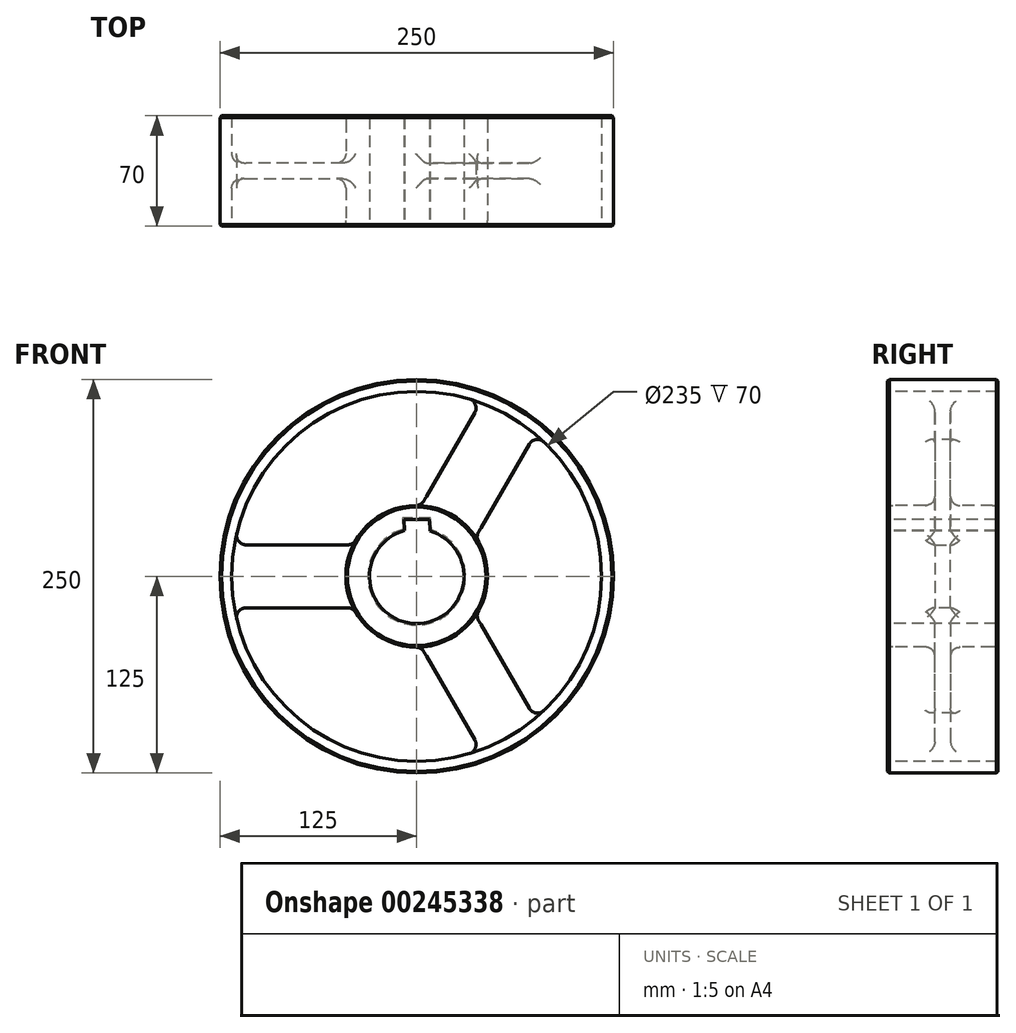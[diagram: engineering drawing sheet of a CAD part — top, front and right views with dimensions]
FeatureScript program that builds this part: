
annotation { "Feature Type Name" : "Feature", "Feature Type Description" : "" }
export const myFeature = defineFeature(function(context is Context, id is Id, definition is map)
    precondition{}
    {
        {
            var Q0;
            Q0=qCreatedBy(makeId("Front.planeOp"),FACE);
            var sketch = newSketch(context, id + "F0", { "sketchPlane" : qUnion([Q0])});
            skCircle(sketch, "E0", {"center": v(0, 0) * mm, "radius": 125 * mm});
            skSolve(sketch);
        }
        {
            var Q0;
            Q0 = qSketchRegion(id + "F0", true);
            extrude(context, id + "F1", {"entities" : qUnion([Q0]), "depth" : 70 * mm});
        }
        {
            var Q0;
            Q0=makeQuery(id+"F1.opExtrude","CAP_FACE",FACE,{"disambiguationData":[OSD([sQuery(id+"F0.wireOp",EDGE,"E0")])],"isStart":false});
            var sketch = newSketch(context, id + "F2", { "sketchPlane" : qUnion([Q0])});
            skCircle(sketch, "E1", {"center": v(0, 0) * mm, "radius": 117.5 * mm});
            skSolve(sketch);
        }
        {
            var Q0;
            Q0 = qSketchRegion(id + "F2", true);
            extrude(context, id + "F3", {"entities" : qUnion([Q0]), "operationType" : NewBodyOperationType.REMOVE, "oppositeDirection" : true, "depth" : 30 * mm});
        }
        {
            var Q0;
            Q0=makeQuery(id+"F1.opExtrude","CAP_FACE",FACE,{"disambiguationData":[OSD([sQuery(id+"F0.wireOp",EDGE,"E0")])],"isStart":true});
            var sketch = newSketch(context, id + "F4", { "sketchPlane" : qUnion([Q0])});
            skCircle(sketch, "E2", {"center": v(0, 0) * mm, "radius": 117.5 * mm});
            skSolve(sketch);
        }
        {
            var Q0;
            Q0 = qSketchRegion(id + "F4", true);
            extrude(context, id + "F5", {"entities" : qUnion([Q0]), "operationType" : NewBodyOperationType.REMOVE, "oppositeDirection" : true, "depth" : 30 * mm});
        }
        {
            var Q0;
            Q0=makeQuery(id+"F5.boolean.opBoolean","COPY",FACE,{"derivedFrom":makeQuery(id+"F5.opExtrude","CAP_FACE",FACE,{"disambiguationData":[OSD([sQuery(id+"F4.wireOp",EDGE,"E2")])],"isStart":false})});
            var sketch = newSketch(context, id + "F6", { "sketchPlane" : qUnion([Q0])});
            skCircle(sketch, "E3", {"center": v(0, 0) * mm, "radius": 45 * mm});
            skSolve(sketch);
        }
        {
            var Q0;
            Q0 = qSketchRegion(id + "F6", true);
            extrude(context, id + "F7", {"entities" : qUnion([Q0]), "operationType" : NewBodyOperationType.ADD, "depth" : 30 * mm});
        }
        {
            var Q0;
            Q0=makeQuery(id+"F3.boolean.opBoolean","COPY",FACE,{"derivedFrom":makeQuery(id+"F3.opExtrude","CAP_FACE",FACE,{"disambiguationData":[OSD([sQuery(id+"F2.wireOp",EDGE,"E1")])],"isStart":false})});
            var sketch = newSketch(context, id + "F8", { "sketchPlane" : qUnion([Q0])});
            skCircle(sketch, "E4", {"center": v(0, 0) * mm, "radius": 45 * mm});
            skSolve(sketch);
        }
        {
            var Q0;
            Q0 = qSketchRegion(id + "F8", true);
            extrude(context, id + "F9", {"entities" : qUnion([Q0]), "operationType" : NewBodyOperationType.ADD, "depth" : 30 * mm});
        }
        {
            var Q0;
            Q0=makeQuery(id+"F9.opExtrude","CAP_FACE",FACE,{"disambiguationData":[OSD([sQuery(id+"F8.wireOp",EDGE,"E4")])],"isStart":false});
            var sketch = newSketch(context, id + "F10", { "sketchPlane" : qUnion([Q0])});
            skArc(sketch, "E5", {"start": v(-7.63, 29.01) * mm, "mid": v(-0.39, -30) * mm, "end": v(8.38, 28.8) * mm});
            skLineSegment(sketch, "E6.bottom", {"start": v(-8, 36) * mm, "end": v(8, 36) * mm});
            skLineSegment(sketch, "E6.left", {"start": v(-8, 36) * mm, "end": v(-7.63, 29.01) * mm});
            skLineSegment(sketch, "E6.right", {"start": v(8, 36) * mm, "end": v(8.38, 28.8) * mm});
            skSolve(sketch);
        }
        {
            var Q0;
            Q0=makeQuery(id+"F10.imprint","IMPRINT",FACE,{"disambiguationData":[TD([[makeQuery(id+"F10.imprint","IMPRINT",EDGE,{"derivedFrom":sQuery(id+"F10.wireOp",EDGE,"E5")}),1.0]])]});
            extrude(context, id + "F11", {"entities" : qUnion([Q0]), "operationType" : NewBodyOperationType.REMOVE, "endBound" : BoundingType.THROUGH_ALL, "oppositeDirection" : true, "depth" : 25 * mm});
        }
        {
            var Q0;
            Q0=makeQuery(id+"F1.opExtrude","CAP_EDGE",EDGE,{"disambiguationData":[OSD([sQuery(id+"F0.wireOp",EDGE,"E0")])],"isStart":false});
            var Q1;
            Q1=makeQuery(id+"F3.boolean.opBoolean","COPY",EDGE,{"derivedFrom":makeQuery(id+"F3.opExtrude","CAP_EDGE",EDGE,{"disambiguationData":[OSD([sQuery(id+"F2.wireOp",EDGE,"E1")])],"isStart":true})});
            var Q2;
            Q2=makeQuery(id+"F9.opExtrude","CAP_EDGE",EDGE,{"disambiguationData":[OSD([sQuery(id+"F8.wireOp",EDGE,"E4")])],"isStart":false});
            var Q3;
            Q3=makeQuery(id+"F11.boolean.opBoolean","COPY",EDGE,{"derivedFrom":makeQuery(id+"F11.opExtrude","CAP_EDGE",EDGE,{"disambiguationData":[OSD([sQuery(id+"F10.wireOp",EDGE,"E5")])],"isStart":true})});
            var Q4;
            Q4=makeQuery(id+"F11.boolean.opBoolean","COPY",EDGE,{"derivedFrom":makeQuery(id+"F11.opExtrude","CAP_EDGE",EDGE,{"disambiguationData":[OSD([sQuery(id+"F10.wireOp",EDGE,"E6.left")])],"isStart":true})});
            var Q5;
            Q5=makeQuery(id+"F11.boolean.opBoolean","COPY",EDGE,{"derivedFrom":makeQuery(id+"F11.opExtrude","CAP_EDGE",EDGE,{"disambiguationData":[OSD([sQuery(id+"F10.wireOp",EDGE,"E6.bottom")])],"isStart":true})});
            var Q6;
            Q6=makeQuery(id+"F11.boolean.opBoolean","COPY",EDGE,{"derivedFrom":makeQuery(id+"F11.opExtrude","CAP_EDGE",EDGE,{"disambiguationData":[OSD([sQuery(id+"F10.wireOp",EDGE,"E6.right")])],"isStart":true})});
            var Q7;
            Q7=makeQuery(id+"F1.opExtrude","CAP_EDGE",EDGE,{"disambiguationData":[OSD([sQuery(id+"F0.wireOp",EDGE,"E0")])],"isStart":true});
            var Q8;
            Q8=makeQuery(id+"F5.boolean.opBoolean","COPY",EDGE,{"derivedFrom":makeQuery(id+"F5.opExtrude","CAP_EDGE",EDGE,{"disambiguationData":[OSD([sQuery(id+"F4.wireOp",EDGE,"E2")])],"isStart":true})});
            var Q9;
            Q9=makeQuery(id+"F7.opExtrude","CAP_EDGE",EDGE,{"disambiguationData":[OSD([sQuery(id+"F6.wireOp",EDGE,"E3")])],"isStart":false});
            var Q10;
            Q10=makeQuery(id+"F11.boolean.opBoolean","INTERSECT",EDGE,{"derivedFrom":[makeQuery(id+"F7.opExtrude","CAP_FACE",FACE,{"disambiguationData":[OSD([sQuery(id+"F6.wireOp",EDGE,"E3")])],"isStart":false}),makeQuery(id+"F11.opExtrude","SWEPT_FACE",FACE,{"disambiguationData":[OSD([sQuery(id+"F10.wireOp",EDGE,"E5")])]})]});
            var Q11;
            Q11=makeQuery(id+"F11.boolean.opBoolean","INTERSECT",EDGE,{"derivedFrom":[makeQuery(id+"F7.opExtrude","CAP_FACE",FACE,{"disambiguationData":[OSD([sQuery(id+"F6.wireOp",EDGE,"E3")])],"isStart":false}),makeQuery(id+"F11.opExtrude","SWEPT_FACE",FACE,{"disambiguationData":[OSD([sQuery(id+"F10.wireOp",EDGE,"E6.right")])]})]});
            var Q12;
            Q12=makeQuery(id+"F11.boolean.opBoolean","INTERSECT",EDGE,{"derivedFrom":[makeQuery(id+"F7.opExtrude","CAP_FACE",FACE,{"disambiguationData":[OSD([sQuery(id+"F6.wireOp",EDGE,"E3")])],"isStart":false}),makeQuery(id+"F11.opExtrude","SWEPT_FACE",FACE,{"disambiguationData":[OSD([sQuery(id+"F10.wireOp",EDGE,"E6.left")])]})]});
            var Q13;
            Q13=makeQuery(id+"F11.boolean.opBoolean","INTERSECT",EDGE,{"derivedFrom":[makeQuery(id+"F7.opExtrude","CAP_FACE",FACE,{"disambiguationData":[OSD([sQuery(id+"F6.wireOp",EDGE,"E3")])],"isStart":false}),makeQuery(id+"F11.opExtrude","SWEPT_FACE",FACE,{"disambiguationData":[OSD([sQuery(id+"F10.wireOp",EDGE,"E6.bottom")])]})]});
            chamfer(context, id + "F12", {"entities" : qUnion([Q0, Q1, Q2, Q3, Q4, Q5, Q6, Q7, Q8, Q9, Q10, Q11, Q12, Q13]), "width" : 1 * mm, "tangentPropagation" : true});
        }
        {
            var Q0;
            Q0=makeQuery(id+"F3.boolean.opBoolean","COPY",FACE,{"derivedFrom":makeQuery(id+"F3.opExtrude","CAP_FACE",FACE,{"disambiguationData":[OSD([sQuery(id+"F2.wireOp",EDGE,"E1")])],"isStart":false})});
            var sketch = newSketch(context, id + "F13", { "sketchPlane" : qUnion([Q0])});
            skCircle(sketch, "E7", {"center": v(0, 0) * mm, "radius": 117.5 * mm});
            skLineSegment(sketch, "E8", {"start": v(-115.79, 20) * mm, "end": v(-40.31, 20) * mm});
            skLineSegment(sketch, "E9", {"start": v(-115.79, -20) * mm, "end": v(-40.31, -20) * mm});
            skArc(sketch, "E10", {"start": v(-40.31, -20) * mm, "mid": v(-45, 0) * mm, "end": v(-40.31, 20) * mm});
            skArc(sketch, "E11", {"start": v(-115.79, 20) * mm, "mid": v(-117.5, 0) * mm, "end": v(-115.79, -20) * mm});
            skArc(sketch, "E12", {"start": v(-115.79, -20) * mm, "mid": v(-117.5, 0) * mm, "end": v(-115.79, 20) * mm});
            skLineSegment(sketch, "E13.1.0", {"start": v(40.57, -110.27) * mm, "end": v(2.84, -44.91) * mm});
            skArc(sketch, "E13.1.1", {"start": v(37.48, -24.91) * mm, "mid": v(22.5, -38.97) * mm, "end": v(2.84, -44.91) * mm});
            skLineSegment(sketch, "E13.1.2", {"start": v(75.21, -90.27) * mm, "end": v(37.48, -24.91) * mm});
            skArc(sketch, "E13.1.3", {"start": v(40.57, -110.27) * mm, "mid": v(58.75, -101.76) * mm, "end": v(75.21, -90.27) * mm});
            skLineSegment(sketch, "E13.2.0", {"start": v(75.21, 90.27) * mm, "end": v(37.48, 24.91) * mm});
            skArc(sketch, "E13.2.1", {"start": v(2.84, 44.91) * mm, "mid": v(22.5, 38.97) * mm, "end": v(37.48, 24.91) * mm});
            skLineSegment(sketch, "E13.2.2", {"start": v(40.57, 110.27) * mm, "end": v(2.84, 44.91) * mm});
            skArc(sketch, "E13.2.3", {"start": v(75.21, 90.27) * mm, "mid": v(58.75, 101.76) * mm, "end": v(40.57, 110.27) * mm});
            skSolve(sketch);
        }
        {
            var Q0;
            {var subQ0=sQuery(id+"F13.wireOp",EDGE,"E13.2.2");Q0=makeQuery(id+"F13.imprint","IMPRINT",FACE,{"disambiguationData":[TD([[makeQuery(id+"F13.imprint","IMPRINT",EDGE,{"derivedFrom":subQ0}),-1.0]])]});}
            var Q1;
            {var subQ0=sQuery(id+"F13.wireOp",EDGE,"E13.1.2");Q1=makeQuery(id+"F13.imprint","IMPRINT",FACE,{"disambiguationData":[TD([[makeQuery(id+"F13.imprint","IMPRINT",EDGE,{"derivedFrom":subQ0}),-1.0]])]});}
            var Q2;
            {var subQ0=sQuery(id+"F13.wireOp",EDGE,"E9");Q2=makeQuery(id+"F13.imprint","IMPRINT",FACE,{"disambiguationData":[TD([[makeQuery(id+"F13.imprint","IMPRINT",EDGE,{"derivedFrom":subQ0}),-1.0]])]});}
            extrude(context, id + "F14", {"entities" : qUnion([Q0, Q1, Q2]), "operationType" : NewBodyOperationType.REMOVE, "endBound" : BoundingType.THROUGH_ALL, "oppositeDirection" : true, "depth" : 25 * mm});
        }
        {
            var Q0;
            {var subQ0=sQuery(id+"F4.wireOp",EDGE,"E2");Q0=makeQuery(id+"F14.boolean.opBoolean","SPLIT",EDGE,{"disambiguationData":[TD([makeQuery(id+"F14.opExtrude","SWEPT_FACE",FACE,{"disambiguationData":[OSD([sQuery(id+"F13.wireOp",EDGE,"E13.1.0")])]})])],"derivedFrom":makeQuery(id+"F5.boolean.opBoolean","COPY",EDGE,{"derivedFrom":makeQuery(id+"F5.opExtrude","CAP_EDGE",EDGE,{"disambiguationData":[OSD([subQ0])],"isStart":false})})});}
            var Q1;
            {var subQ0=sQuery(id+"F6.wireOp",EDGE,"E3");Q1=makeQuery(id+"F14.boolean.opBoolean","SPLIT",EDGE,{"disambiguationData":[TD([makeQuery(id+"F14.opExtrude","SWEPT_FACE",FACE,{"disambiguationData":[OSD([sQuery(id+"F13.wireOp",EDGE,"E13.2.0")])]})])],"derivedFrom":makeQuery(id+"F7.opExtrude","CAP_EDGE",EDGE,{"disambiguationData":[OSD([subQ0])],"isStart":true})});}
            var Q2;
            {var subQ0=sQuery(id+"F6.wireOp",EDGE,"E3");Q2=makeQuery(id+"F14.boolean.opBoolean","SPLIT",EDGE,{"disambiguationData":[TD([makeQuery(id+"F14.opExtrude","SWEPT_FACE",FACE,{"disambiguationData":[OSD([sQuery(id+"F13.wireOp",EDGE,"E8")])]})])],"derivedFrom":makeQuery(id+"F7.opExtrude","CAP_EDGE",EDGE,{"disambiguationData":[OSD([subQ0])],"isStart":true})});}
            var Q3;
            {var subQ0=sQuery(id+"F4.wireOp",EDGE,"E2");Q3=makeQuery(id+"F14.boolean.opBoolean","SPLIT",EDGE,{"disambiguationData":[TD([makeQuery(id+"F14.opExtrude","SWEPT_FACE",FACE,{"disambiguationData":[OSD([sQuery(id+"F13.wireOp",EDGE,"E13.2.0")])]})])],"derivedFrom":makeQuery(id+"F5.boolean.opBoolean","COPY",EDGE,{"derivedFrom":makeQuery(id+"F5.opExtrude","CAP_EDGE",EDGE,{"disambiguationData":[OSD([subQ0])],"isStart":false})})});}
            var Q4;
            {var subQ0=sQuery(id+"F4.wireOp",EDGE,"E2");Q4=makeQuery(id+"F14.boolean.opBoolean","SPLIT",EDGE,{"disambiguationData":[TD([makeQuery(id+"F14.opExtrude","SWEPT_FACE",FACE,{"disambiguationData":[OSD([sQuery(id+"F13.wireOp",EDGE,"E8")])]})])],"derivedFrom":makeQuery(id+"F5.boolean.opBoolean","COPY",EDGE,{"derivedFrom":makeQuery(id+"F5.opExtrude","CAP_EDGE",EDGE,{"disambiguationData":[OSD([subQ0])],"isStart":false})})});}
            var Q5;
            {var subQ0=sQuery(id+"F6.wireOp",EDGE,"E3");Q5=makeQuery(id+"F14.boolean.opBoolean","SPLIT",EDGE,{"disambiguationData":[TD([makeQuery(id+"F14.opExtrude","SWEPT_FACE",FACE,{"disambiguationData":[OSD([sQuery(id+"F13.wireOp",EDGE,"E13.1.0")])]})])],"derivedFrom":makeQuery(id+"F7.opExtrude","CAP_EDGE",EDGE,{"disambiguationData":[OSD([subQ0])],"isStart":true})});}
            fillet(context, id + "F15", {"entities" : qUnion([Q0, Q1, Q2, Q3, Q4, Q5]), "radius" : 6 * mm, "tangentPropagation" : true, "allowEdgeOverflow" : false});
        }
        {
            var Q0;
            {var subQ0=sQuery(id+"F2.wireOp",EDGE,"E1");var subQ1=sQuery(id+"F13.wireOp",EDGE,"E8");Q0=makeQuery(id+"F14.boolean.opBoolean","SPLIT",EDGE,{"disambiguationData":[TD([makeQuery(id+"F14.opExtrude","SWEPT_FACE",FACE,{"disambiguationData":[OSD([subQ1])]})])],"derivedFrom":makeQuery(id+"F3.boolean.opBoolean","COPY",EDGE,{"derivedFrom":makeQuery(id+"F3.opExtrude","CAP_EDGE",EDGE,{"disambiguationData":[OSD([subQ0])],"isStart":false})})});}
            var Q1;
            {var subQ0=sQuery(id+"F2.wireOp",EDGE,"E1");var subQ2=sQuery(id+"F13.wireOp",EDGE,"E13.1.0");Q1=makeQuery(id+"F14.boolean.opBoolean","SPLIT",EDGE,{"disambiguationData":[TD([makeQuery(id+"F14.opExtrude","SWEPT_FACE",FACE,{"disambiguationData":[OSD([subQ2])]})])],"derivedFrom":makeQuery(id+"F3.boolean.opBoolean","COPY",EDGE,{"derivedFrom":makeQuery(id+"F3.opExtrude","CAP_EDGE",EDGE,{"disambiguationData":[OSD([subQ0])],"isStart":false})})});}
            var Q2;
            {var subQ0=sQuery(id+"F13.wireOp",EDGE,"E13.2.0");var subQ2=sQuery(id+"F8.wireOp",EDGE,"E4");var subQ4=makeQuery(id+"F9.opExtrude","CAP_EDGE",EDGE,{"disambiguationData":[OSD([subQ2])],"isStart":true});Q2=makeQuery(id+"F14.boolean.opBoolean","SPLIT",EDGE,{"disambiguationData":[TD([makeQuery(id+"F14.opExtrude","SWEPT_FACE",FACE,{"disambiguationData":[OSD([subQ0])]})])],"derivedFrom":subQ4});}
            var Q3;
            Q3=makeQuery(id+"F14.boolean.opBoolean","COPY",EDGE,{"derivedFrom":makeQuery(id+"F14.opExtrude","SWEPT_EDGE",EDGE,{"disambiguationData":[OSD([sQuery(id+"F13.wireOp",EDGE,"E7"),sQuery(id+"F13.wireOp",EDGE,"E8")])]})});
            var Q4;
            Q4=makeQuery(id+"F14.boolean.opBoolean","COPY",EDGE,{"derivedFrom":makeQuery(id+"F14.opExtrude","SWEPT_EDGE",EDGE,{"disambiguationData":[OSD([sQuery(id+"F8.wireOp",EDGE,"E4"),sQuery(id+"F13.wireOp",EDGE,"E13.2.0"),sQuery(id+"F13.wireOp",EDGE,"E13.2.1")])]})});
            var Q5;
            Q5=makeQuery(id+"F14.boolean.opBoolean","COPY",EDGE,{"derivedFrom":makeQuery(id+"F14.opExtrude","SWEPT_EDGE",EDGE,{"disambiguationData":[OSD([sQuery(id+"F8.wireOp",EDGE,"E4"),sQuery(id+"F13.wireOp",EDGE,"E13.1.1"),sQuery(id+"F13.wireOp",EDGE,"E13.1.2")])]})});
            var Q6;
            {var subQ0=sQuery(id+"F13.wireOp",EDGE,"E13.1.0");var subQ1=sQuery(id+"F8.wireOp",EDGE,"E4");var subQ4=makeQuery(id+"F9.opExtrude","CAP_EDGE",EDGE,{"disambiguationData":[OSD([subQ1])],"isStart":true});Q6=makeQuery(id+"F14.boolean.opBoolean","SPLIT",EDGE,{"disambiguationData":[TD([makeQuery(id+"F14.opExtrude","SWEPT_FACE",FACE,{"disambiguationData":[OSD([subQ0])]})])],"derivedFrom":subQ4});}
            var Q7;
            Q7=makeQuery(id+"F14.boolean.opBoolean","COPY",EDGE,{"derivedFrom":makeQuery(id+"F14.opExtrude","SWEPT_EDGE",EDGE,{"disambiguationData":[OSD([sQuery(id+"F13.wireOp",EDGE,"E7"),sQuery(id+"F13.wireOp",EDGE,"E9")])]})});
            var Q8;
            {var subQ0=sQuery(id+"F13.wireOp",EDGE,"E13.2.0");var subQ1=sQuery(id+"F2.wireOp",EDGE,"E1");Q8=makeQuery(id+"F14.boolean.opBoolean","SPLIT",EDGE,{"disambiguationData":[TD([makeQuery(id+"F14.opExtrude","SWEPT_FACE",FACE,{"disambiguationData":[OSD([subQ0])]})])],"derivedFrom":makeQuery(id+"F3.boolean.opBoolean","COPY",EDGE,{"derivedFrom":makeQuery(id+"F3.opExtrude","CAP_EDGE",EDGE,{"disambiguationData":[OSD([subQ1])],"isStart":false})})});}
            var Q9;
            Q9=makeQuery(id+"F14.boolean.opBoolean","COPY",EDGE,{"derivedFrom":makeQuery(id+"F14.opExtrude","SWEPT_EDGE",EDGE,{"disambiguationData":[OSD([sQuery(id+"F13.wireOp",EDGE,"E7"),sQuery(id+"F13.wireOp",EDGE,"E13.2.0")])]})});
            var Q10;
            Q10=makeQuery(id+"F14.boolean.opBoolean","COPY",EDGE,{"derivedFrom":makeQuery(id+"F14.opExtrude","SWEPT_EDGE",EDGE,{"disambiguationData":[OSD([sQuery(id+"F8.wireOp",EDGE,"E4"),sQuery(id+"F13.wireOp",EDGE,"E8"),sQuery(id+"F13.wireOp",EDGE,"E10")])]})});
            var Q11;
            Q11=makeQuery(id+"F14.boolean.opBoolean","COPY",EDGE,{"derivedFrom":makeQuery(id+"F14.opExtrude","SWEPT_EDGE",EDGE,{"disambiguationData":[OSD([sQuery(id+"F13.wireOp",EDGE,"E7"),sQuery(id+"F13.wireOp",EDGE,"E13.1.0")])]})});
            var Q12;
            Q12=makeQuery(id+"F14.boolean.opBoolean","COPY",EDGE,{"derivedFrom":makeQuery(id+"F14.opExtrude","SWEPT_EDGE",EDGE,{"disambiguationData":[OSD([sQuery(id+"F13.wireOp",EDGE,"E7"),sQuery(id+"F13.wireOp",EDGE,"E13.2.2")])]})});
            var Q13;
            Q13=makeQuery(id+"F14.boolean.opBoolean","COPY",EDGE,{"derivedFrom":makeQuery(id+"F14.opExtrude","SWEPT_EDGE",EDGE,{"disambiguationData":[OSD([sQuery(id+"F8.wireOp",EDGE,"E4"),sQuery(id+"F13.wireOp",EDGE,"E13.1.0"),sQuery(id+"F13.wireOp",EDGE,"E13.1.1")])]})});
            var Q14;
            Q14=makeQuery(id+"F14.boolean.opBoolean","COPY",EDGE,{"derivedFrom":makeQuery(id+"F14.opExtrude","SWEPT_EDGE",EDGE,{"disambiguationData":[OSD([sQuery(id+"F8.wireOp",EDGE,"E4"),sQuery(id+"F13.wireOp",EDGE,"E9"),sQuery(id+"F13.wireOp",EDGE,"E10")])]})});
            var Q15;
            {var subQ0=sQuery(id+"F13.wireOp",EDGE,"E13.1.1");var subQ1=sQuery(id+"F8.wireOp",EDGE,"E4");var subQ2=makeQuery(id+"F9.opExtrude","CAP_EDGE",EDGE,{"disambiguationData":[OSD([subQ1])],"isStart":true});var subQ4=sQuery(id+"F13.wireOp",EDGE,"E10");Q15=makeQuery(id+"F14.boolean.opBoolean","MERGE",FACE,{"derivedFrom":[makeQuery(id+"F7.opExtrude","SWEPT_FACE",FACE,{"disambiguationData":[OSD([sQuery(id+"F6.wireOp",EDGE,"E3")])]}),makeQuery(id+"F9.opExtrude","SWEPT_FACE",FACE,{"disambiguationData":[OSD([subQ1])]}),makeQuery(id+"F14.opExtrude","SWEPT_FACE",FACE,{"disambiguationData":[OSD([subQ1]),TDD([makeQuery(id+"F13.imprint","IMPRINT",EDGE,{"disambiguationData":[TD([[makeQuery(id+"F13.imprint","INTERSECT",VERTEX,{"derivedFrom":[subQ2,sQuery(id+"F13.wireOp",EDGE,"E8"),subQ4]}),1.0]])],"derivedFrom":subQ2})])]}),makeQuery(id+"F14.opExtrude","SWEPT_FACE",FACE,{"disambiguationData":[OSD([subQ1]),TDD([makeQuery(id+"F13.imprint","IMPRINT",EDGE,{"disambiguationData":[TD([[makeQuery(id+"F13.imprint","INTERSECT",VERTEX,{"derivedFrom":[subQ2,sQuery(id+"F13.wireOp",EDGE,"E9"),subQ4]}),-1.0]])],"derivedFrom":subQ2})])]}),makeQuery(id+"F14.opExtrude","SWEPT_FACE",FACE,{"disambiguationData":[OSD([subQ1]),TDD([makeQuery(id+"F13.imprint","IMPRINT",EDGE,{"disambiguationData":[TD([[makeQuery(id+"F13.imprint","INTERSECT",VERTEX,{"derivedFrom":[subQ2,subQ0,sQuery(id+"F13.wireOp",EDGE,"E13.1.2")]}),-1.0]])],"derivedFrom":subQ2})])]})]});}
            var Q16;
            Q16=makeQuery(id+"F14.boolean.opBoolean","COPY",EDGE,{"derivedFrom":makeQuery(id+"F14.opExtrude","SWEPT_EDGE",EDGE,{"disambiguationData":[OSD([sQuery(id+"F8.wireOp",EDGE,"E4"),sQuery(id+"F13.wireOp",EDGE,"E13.2.1"),sQuery(id+"F13.wireOp",EDGE,"E13.2.2")])]})});
            var Q17;
            Q17=makeQuery(id+"F14.boolean.opBoolean","COPY",EDGE,{"derivedFrom":makeQuery(id+"F14.opExtrude","SWEPT_EDGE",EDGE,{"disambiguationData":[OSD([sQuery(id+"F13.wireOp",EDGE,"E7"),sQuery(id+"F13.wireOp",EDGE,"E13.1.2")])]})});
            fillet(context, id + "F16", {"entities" : qUnion([Q0, Q1, Q2, Q3, Q4, Q5, Q6, Q7, Q8, Q9, Q10, Q11, Q12, Q13, Q14, Q15, Q16, Q17]), "radius" : 6 * mm, "tangentPropagation" : true, "allowEdgeOverflow" : false});
        }
    });
